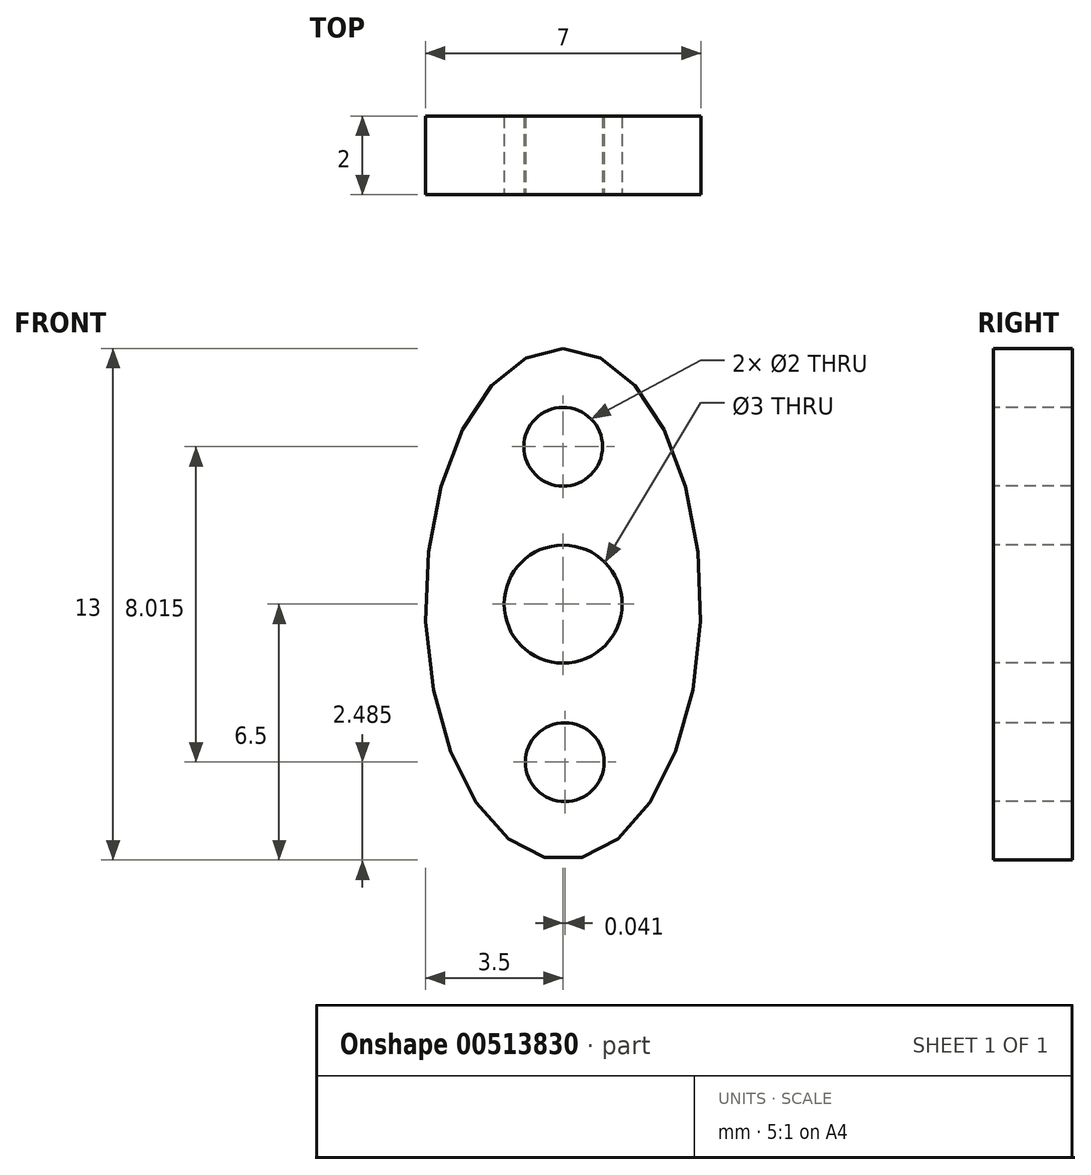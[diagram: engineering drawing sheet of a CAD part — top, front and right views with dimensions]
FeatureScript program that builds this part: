
annotation { "Feature Type Name" : "Feature", "Feature Type Description" : "" }
export const myFeature = defineFeature(function(context is Context, id is Id, definition is map)
    precondition{}
    {
        {
            var Q0;
            Q0=qCreatedBy(makeId("Front.planeOp"),FACE);
            var sketch = newSketch(context, id + "F0", { "sketchPlane" : qUnion([Q0])});
            skLineSegment(sketch, "E0", {"start": v(0, 6.5) * mm, "end": v(0, -6.5) * mm, "construction": true});
            skLineSegment(sketch, "E1", {"start": v(-3.5, 0) * mm, "end": v(3.5, 0) * mm, "construction": true});
            skPoint(sketch, "E2", {"position": v(0, 0) * mm});
            skCircle(sketch, "E3", {"center": v(0, 0) * mm, "radius": 1.5 * mm});
            skPoint(sketch, "E4", {"position": v(0, 4) * mm});
            skPoint(sketch, "E5", {"position": v(0, -4) * mm});
            skCircle(sketch, "E6", {"center": v(0, 4) * mm, "radius": 1 * mm});
            skCircle(sketch, "E7", {"center": v(0.04, -4.02) * mm, "radius": 1 * mm});
            skEllipse(sketch, "E8", {"center": v(0, 0) * mm, "majorRadius": 6.5 * mm, "minorRadius": 3.5 * mm, "majorAxis": v(0, 1)});
            skSolve(sketch);
        }
        {
            var Q0;
            Q0=makeQuery(id+"F0.imprint","IMPRINT",FACE,{"disambiguationData":[TD([[makeQuery(id+"F0.imprint","IMPRINT",EDGE,{"derivedFrom":sQuery(id+"F0.wireOp",EDGE,"E3")}),-1.0]])]});
            extrude(context, id + "F1", {"entities" : qUnion([Q0]), "oppositeDirection" : true, "depth" : 2 * mm});
        }
    });
